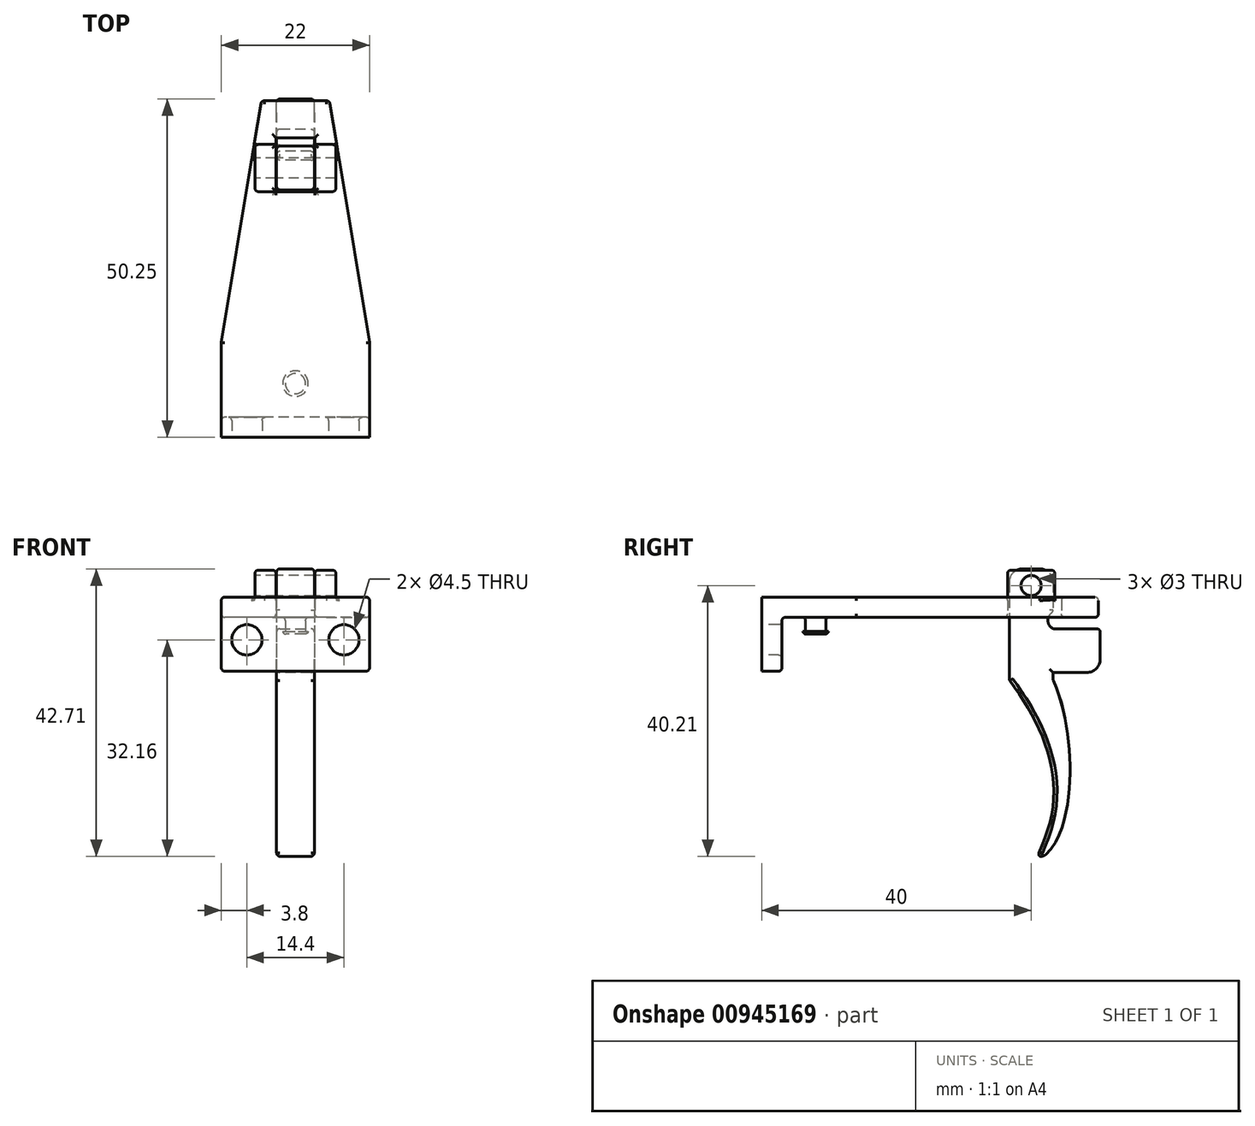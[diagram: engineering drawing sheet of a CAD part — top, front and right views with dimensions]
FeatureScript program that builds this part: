
annotation { "Feature Type Name" : "Feature", "Feature Type Description" : "" }
export const myFeature = defineFeature(function(context is Context, id is Id, definition is map)
    precondition{}
    {
        {
            var Q0;
            Q0=qCreatedBy(makeId("Right.planeOp"),FACE);
            var sketch = newSketch(context, id + "F0", { "sketchPlane" : qUnion([Q0])});
            skLineSegment(sketch, "E0", {"start": v(-37, -4.7) * mm, "end": v(-37, -12.7) * mm});
            skLineSegment(sketch, "E1", {"start": v(-37, -12.7) * mm, "end": v(-40, -12.7) * mm});
            skLineSegment(sketch, "E2", {"start": v(-40, -12.7) * mm, "end": v(-40, -1.7) * mm});
            skLineSegment(sketch, "E3", {"start": v(-40, -1.7) * mm, "end": v(10, -1.7) * mm});
            skLineSegment(sketch, "E4", {"start": v(10, -1.7) * mm, "end": v(10, -4.7) * mm});
            skLineSegment(sketch, "E5", {"start": v(10, -4.7) * mm, "end": v(-37, -4.7) * mm});
            skLineSegment(sketch, "E6", {"start": v(-3.5, -1.7) * mm, "end": v(-3.5, 2.3) * mm});
            skLineSegment(sketch, "E7", {"start": v(-3.5, 2.3) * mm, "end": v(3.5, 2.3) * mm});
            skLineSegment(sketch, "E8", {"start": v(3.5, 2.3) * mm, "end": v(3.5, -1.7) * mm});
            skCircle(sketch, "E9", {"center": v(0, 0) * mm, "radius": 1.5 * mm});
            skLineSegment(sketch, "E10", {"start": v(-33.5, -4.7) * mm, "end": v(-33.5, -6.8) * mm});
            skLineSegment(sketch, "E11", {"start": v(-33.5, -6.8) * mm, "end": v(-33.9, -6.8) * mm});
            skLineSegment(sketch, "E12", {"start": v(-33.9, -6.8) * mm, "end": v(-33.9, -7.2) * mm});
            skLineSegment(sketch, "E13", {"start": v(-33.9, -7.2) * mm, "end": v(-32, -7.2) * mm});
            skPoint(sketch, "E14.startSnap0", {"position": v(-32, -7.2) * mm});
            skLineSegment(sketch, "E15", {"start": v(-33.5, -4.7) * mm, "end": v(-30.5, -4.7) * mm});
            skLineSegment(sketch, "E16", {"start": v(-32, -7.2) * mm, "end": v(-32, -4.7) * mm});
            skSolve(sketch);
        }
        {
            var Q0;
            Q0=qCreatedBy(makeId("Right.planeOp"),FACE);
            var sketch = newSketch(context, id + "F1", { "sketchPlane" : qUnion([Q0])});
            skLineSegment(sketch, "E17", {"start": v(-3.25, 2.5) * mm, "end": v(3.25, 2.5) * mm});
            skLineSegment(sketch, "E18", {"start": v(3.25, 2.5) * mm, "end": v(3.25, -3.9) * mm});
            skLineSegment(sketch, "E19", {"start": v(3.25, -6.4) * mm, "end": v(10.25, -6.4) * mm});
            skLineSegment(sketch, "E20", {"start": v(10.25, -6.4) * mm, "end": v(10.25, -12.9) * mm});
            skLineSegment(sketch, "E21", {"start": v(10.25, -12.9) * mm, "end": v(3.25, -12.9) * mm});
            skLineSegment(sketch, "E22", {"start": v(3.25, -12.9) * mm, "end": v(3.25, -14) * mm});
            skLineSegment(sketch, "E23", {"start": v(-3.25, 2.5) * mm, "end": v(-3.25, -14) * mm});
            skFitSpline(sketch, "E24", {"points": [v(3.25, -14) * mm, v(2.1, -40) * mm], "startDerivative": vector(10.65, -23.23) * mm, "endDerivative": vector(-14.09, -12.06) * mm});
            skLineSegment(sketch, "E25", {"start": v(-3.25, -14) * mm, "end": v(-3.25, -43.38) * mm, "construction": true});
            skLineSegment(sketch, "E26", {"start": v(3.25, -14) * mm, "end": v(3.25, -43.8) * mm, "construction": true});
            skFitSpline(sketch, "E27", {"points": [v(-3.25, -14) * mm, v(1.15, -40) * mm, v(2.1, -40) * mm], "startDerivative": vector(42.39, -56.19) * mm, "endDerivative": vector(10.15, 5.19) * mm});
            skPoint(sketch, "E28", {"position": v(5.75, -28.9) * mm});
            skPoint(sketch, "E28.positionSnap0", {"position": v(3.25, -28.9) * mm});
            skCircle(sketch, "E29", {"center": v(0, 0) * mm, "radius": 1.5 * mm});
            skArc(sketch, "E30", {"start": v(3.25, -3.9) * mm, "mid": v(2.49, -5.15) * mm, "end": v(3.25, -6.4) * mm});
            skLineSegment(sketch, "E31.trimOffspring", {"start": v(3.25, -6.4) * mm, "end": v(3.25, -6.4) * mm});
            skSolve(sketch);
        }
        {
            var Q0;
            Q0=makeQuery(id+"F0.imprint","IMPRINT",FACE,{"disambiguationData":[TD([[makeQuery(id+"F0.imprint","IMPRINT",EDGE,{"derivedFrom":sQuery(id+"F0.wireOp",EDGE,"E0")}),-1.0]])]});
            extrude(context, id + "F2", {"entities" : qUnion([Q0]), "endBound" : BoundingType.SYMMETRIC, "depth" : 22 * mm, "offsetDistance" : 25 * mm});
        }
        {
            var Q0;
            {var subQ1=sQuery(id+"F0.wireOp",EDGE,"E6");Q0=makeQuery(id+"F0.imprint","IMPRINT",FACE,{"disambiguationData":[TD([[makeQuery(id+"F0.imprint","IMPRINT",EDGE,{"derivedFrom":subQ1}),-1.0]])]});}
            extrude(context, id + "F3", {"entities" : qUnion([Q0]), "operationType" : NewBodyOperationType.ADD, "endBound" : BoundingType.SYMMETRIC, "depth" : 12 * mm, "offsetDistance" : 25 * mm});
        }
        {
            var Q0;
            Q0=qCreatedBy(makeId("Right.planeOp"),FACE);
            var sketch = newSketch(context, id + "F4", { "sketchPlane" : qUnion([Q0])});
            skLineSegment(sketch, "E32.bottom", {"start": v(-3.5, 4) * mm, "end": v(4.5, 4) * mm});
            skLineSegment(sketch, "E32.top", {"start": v(-3.5, -6) * mm, "end": v(4.5, -6) * mm});
            skLineSegment(sketch, "E32.left", {"start": v(-3.5, 4) * mm, "end": v(-3.5, -6) * mm});
            skLineSegment(sketch, "E32.right", {"start": v(4.5, 4) * mm, "end": v(4.5, -6) * mm});
            skSolve(sketch);
        }
        {
            var Q0;
            Q0 = qSketchRegion(id + "F4", true);
            extrude(context, id + "F5", {"entities" : qUnion([Q0]), "operationType" : NewBodyOperationType.REMOVE, "endBound" : BoundingType.SYMMETRIC, "depth" : 5.8 * mm, "offsetDistance" : 25 * mm});
        }
        {
            var Q0;
            Q0 = qSketchRegion(id + "F1", true);
            extrude(context, id + "F6", {"entities" : qUnion([Q0]), "endBound" : BoundingType.SYMMETRIC, "depth" : 5.6 * mm, "offsetDistance" : 25 * mm});
        }
        {
            var Q0;
            Q0=makeQuery(id+"F1.imprint","IMPRINT",FACE,{"disambiguationData":[TD([[makeQuery(id+"F1.imprint","IMPRINT",EDGE,{"derivedFrom":sQuery(id+"F1.wireOp",EDGE,"E29")}),1.0]])]});
            extrude(context, id + "F7", {"entities" : qUnion([Q0]), "operationType" : NewBodyOperationType.REMOVE, "endBound" : BoundingType.SYMMETRIC, "depth" : 12 * mm, "offsetDistance" : 25 * mm});
        }
        {
            var Q0;
            Q0=makeQuery(id+"F6.opExtrude","SWEPT_EDGE",EDGE,{"disambiguationData":[OSD([sQuery(id+"F1.wireOp",EDGE,"E17"),sQuery(id+"F1.wireOp",EDGE,"E23")])]});
            var Q1;
            Q1=makeQuery(id+"F6.opExtrude","SWEPT_EDGE",EDGE,{"disambiguationData":[OSD([sQuery(id+"F1.wireOp",EDGE,"E17"),sQuery(id+"F1.wireOp",EDGE,"E18")])]});
            var Q2;
            Q2=makeQuery(id+"F6.opExtrude","SWEPT_EDGE",EDGE,{"disambiguationData":[OSD([sQuery(id+"F1.wireOp",EDGE,"E20"),sQuery(id+"F1.wireOp",EDGE,"E21")])]});
            fillet(context, id + "F8", {"entities" : qUnion([Q0, Q1, Q2]), "radius" : 2 * mm, "tangentPropagation" : true, "allowEdgeOverflow" : false});
        }
        {
            var Q0;
            Q0=makeQuery(id+"F6.opExtrude","CAP_EDGE",EDGE,{"disambiguationData":[OSD([sQuery(id+"F1.wireOp",EDGE,"E23")])],"isStart":true});
            var Q1;
            Q1=makeQuery(id+"F6.opExtrude","CAP_EDGE",EDGE,{"disambiguationData":[OSD([sQuery(id+"F1.wireOp",EDGE,"E27")])],"isStart":false});
            var Q2;
            Q2=makeQuery(id+"F6.opExtrude","CAP_EDGE",EDGE,{"disambiguationData":[OSD([sQuery(id+"F1.wireOp",EDGE,"E27")])],"isStart":true});
            var Q3;
            Q3=makeQuery(id+"F6.opExtrude","CAP_EDGE",EDGE,{"disambiguationData":[OSD([sQuery(id+"F1.wireOp",EDGE,"E24")])],"isStart":false});
            var Q4;
            Q4=makeQuery(id+"F6.opExtrude","CAP_EDGE",EDGE,{"disambiguationData":[OSD([sQuery(id+"F1.wireOp",EDGE,"E24")])],"isStart":true});
            var Q5;
            Q5=makeQuery(id+"F6.opExtrude","SWEPT_EDGE",EDGE,{"disambiguationData":[OSD([sQuery(id+"F1.wireOp",EDGE,"E22"),sQuery(id+"F1.wireOp",EDGE,"E24")])]});
            var Q6;
            Q6=makeQuery(id+"F6.opExtrude","SWEPT_EDGE",EDGE,{"disambiguationData":[OSD([sQuery(id+"F1.wireOp",EDGE,"E24"),sQuery(id+"F1.wireOp",EDGE,"E27")])]});
            var Q7;
            Q7=makeQuery(id+"F6.opExtrude","CAP_EDGE",EDGE,{"disambiguationData":[OSD([sQuery(id+"F1.wireOp",EDGE,"E23")])],"isStart":false});
            var Q8;
            Q8=makeQuery(id+"F6.opExtrude","SWEPT_EDGE",EDGE,{"disambiguationData":[OSD([sQuery(id+"F1.wireOp",EDGE,"E19"),sQuery(id+"F1.wireOp",EDGE,"E20")])]});
            var Q9;
            {var subQ0=sQuery(id+"F1.wireOp",EDGE,"E21");var subQ1=sQuery(id+"F1.wireOp",EDGE,"E20");Q9=makeQuery(id+"F8.opFillet","BLEND_EDGE",EDGE,{"blendedFrom":[makeQuery(id+"F6.opExtrude","SWEPT_EDGE",EDGE,{"disambiguationData":[OSD([subQ1,subQ0])]}),makeQuery(id+"F6.opExtrude","CAP_FACE",FACE,{"disambiguationData":[OSD([sQuery(id+"F1.wireOp",EDGE,"E17"),sQuery(id+"F1.wireOp",EDGE,"E18"),sQuery(id+"F1.wireOp",EDGE,"E19"),subQ1,subQ0,sQuery(id+"F1.wireOp",EDGE,"E22"),sQuery(id+"F1.wireOp",EDGE,"E23"),sQuery(id+"F1.wireOp",EDGE,"E24"),sQuery(id+"F1.wireOp",EDGE,"E27"),sQuery(id+"F1.wireOp",EDGE,"E29")])],"isStart":false})],"blendedInto":[makeQuery(id+"F6.opExtrude","CAP_FACE",FACE,{"disambiguationData":[OSD([sQuery(id+"F1.wireOp",EDGE,"E17"),sQuery(id+"F1.wireOp",EDGE,"E18"),sQuery(id+"F1.wireOp",EDGE,"E19"),subQ1,subQ0,sQuery(id+"F1.wireOp",EDGE,"E22"),sQuery(id+"F1.wireOp",EDGE,"E23"),sQuery(id+"F1.wireOp",EDGE,"E24"),sQuery(id+"F1.wireOp",EDGE,"E27"),sQuery(id+"F1.wireOp",EDGE,"E29")])],"isStart":false})]});}
            var Q10;
            Q10=makeQuery(id+"F6.opExtrude","CAP_EDGE",EDGE,{"disambiguationData":[OSD([sQuery(id+"F1.wireOp",EDGE,"E20")])],"isStart":false});
            var Q11;
            {var subQ0=sQuery(id+"F1.wireOp",EDGE,"E21");var subQ1=sQuery(id+"F1.wireOp",EDGE,"E20");Q11=makeQuery(id+"F8.opFillet","BLEND_EDGE",EDGE,{"blendedFrom":[makeQuery(id+"F6.opExtrude","SWEPT_EDGE",EDGE,{"disambiguationData":[OSD([subQ1,subQ0])]}),makeQuery(id+"F6.opExtrude","CAP_FACE",FACE,{"disambiguationData":[OSD([sQuery(id+"F1.wireOp",EDGE,"E17"),sQuery(id+"F1.wireOp",EDGE,"E18"),sQuery(id+"F1.wireOp",EDGE,"E19"),subQ1,subQ0,sQuery(id+"F1.wireOp",EDGE,"E22"),sQuery(id+"F1.wireOp",EDGE,"E23"),sQuery(id+"F1.wireOp",EDGE,"E24"),sQuery(id+"F1.wireOp",EDGE,"E27"),sQuery(id+"F1.wireOp",EDGE,"E29")])],"isStart":true})],"blendedInto":[makeQuery(id+"F6.opExtrude","CAP_FACE",FACE,{"disambiguationData":[OSD([sQuery(id+"F1.wireOp",EDGE,"E17"),sQuery(id+"F1.wireOp",EDGE,"E18"),sQuery(id+"F1.wireOp",EDGE,"E19"),subQ1,subQ0,sQuery(id+"F1.wireOp",EDGE,"E22"),sQuery(id+"F1.wireOp",EDGE,"E23"),sQuery(id+"F1.wireOp",EDGE,"E24"),sQuery(id+"F1.wireOp",EDGE,"E27"),sQuery(id+"F1.wireOp",EDGE,"E29")])],"isStart":true})]});}
            var Q12;
            {var subQ0=sQuery(id+"F1.wireOp",EDGE,"E17");Q12=makeQuery(id+"F8.opFillet","BLEND_EDGE",EDGE,{"blendedFrom":[makeQuery(id+"F6.opExtrude","SWEPT_EDGE",EDGE,{"disambiguationData":[OSD([subQ0,sQuery(id+"F1.wireOp",EDGE,"E23")])]}),makeQuery(id+"F6.opExtrude","SWEPT_EDGE",EDGE,{"disambiguationData":[OSD([subQ0,sQuery(id+"F1.wireOp",EDGE,"E18")])]})],"blendedInto":[]});}
            var Q13;
            Q13=makeQuery(id+"F7.opExtrude","CAP_EDGE",EDGE,{"disambiguationData":[OSD([sQuery(id+"F1.wireOp",EDGE,"E29")])],"isStart":false});
            var Q14;
            Q14=makeQuery(id+"F7.opExtrude","CAP_EDGE",EDGE,{"disambiguationData":[OSD([sQuery(id+"F1.wireOp",EDGE,"E29")])],"isStart":true});
            var Q15;
            {var subQ1=sQuery(id+"F0.wireOp",EDGE,"E7");var subQ2=sQuery(id+"F0.wireOp",EDGE,"E6");Q15=makeQuery(id+"F5.boolean.opBoolean","SPLIT",EDGE,{"disambiguationData":[TD([makeQuery(id+"F5.opExtrude","CAP_FACE",FACE,{"disambiguationData":[OSD([sQuery(id+"F4.wireOp",EDGE,"E32.bottom"),sQuery(id+"F4.wireOp",EDGE,"E32.top"),sQuery(id+"F4.wireOp",EDGE,"E32.left"),sQuery(id+"F4.wireOp",EDGE,"E32.right")])],"isStart":true})])],"derivedFrom":makeQuery(id+"F3.opExtrude","SWEPT_EDGE",EDGE,{"disambiguationData":[OSD([subQ2,subQ1])]})});}
            var Q16;
            {var subQ1=sQuery(id+"F0.wireOp",EDGE,"E8");var subQ2=sQuery(id+"F0.wireOp",EDGE,"E7");Q16=makeQuery(id+"F5.boolean.opBoolean","SPLIT",EDGE,{"disambiguationData":[TD([makeQuery(id+"F5.opExtrude","CAP_FACE",FACE,{"disambiguationData":[OSD([sQuery(id+"F4.wireOp",EDGE,"E32.bottom"),sQuery(id+"F4.wireOp",EDGE,"E32.top"),sQuery(id+"F4.wireOp",EDGE,"E32.left"),sQuery(id+"F4.wireOp",EDGE,"E32.right")])],"isStart":true})])],"derivedFrom":makeQuery(id+"F3.opExtrude","SWEPT_EDGE",EDGE,{"disambiguationData":[OSD([subQ2,subQ1])]})});}
            var Q17;
            {var subQ1=sQuery(id+"F0.wireOp",EDGE,"E8");var subQ2=sQuery(id+"F0.wireOp",EDGE,"E7");Q17=makeQuery(id+"F5.boolean.opBoolean","SPLIT",EDGE,{"disambiguationData":[TD([makeQuery(id+"F5.opExtrude","CAP_FACE",FACE,{"disambiguationData":[OSD([sQuery(id+"F4.wireOp",EDGE,"E32.bottom"),sQuery(id+"F4.wireOp",EDGE,"E32.top"),sQuery(id+"F4.wireOp",EDGE,"E32.left"),sQuery(id+"F4.wireOp",EDGE,"E32.right")])],"isStart":false})])],"derivedFrom":makeQuery(id+"F3.opExtrude","SWEPT_EDGE",EDGE,{"disambiguationData":[OSD([subQ2,subQ1])]})});}
            var Q18;
            {var subQ1=sQuery(id+"F0.wireOp",EDGE,"E7");var subQ2=sQuery(id+"F0.wireOp",EDGE,"E6");Q18=makeQuery(id+"F5.boolean.opBoolean","SPLIT",EDGE,{"disambiguationData":[TD([makeQuery(id+"F5.opExtrude","CAP_FACE",FACE,{"disambiguationData":[OSD([sQuery(id+"F4.wireOp",EDGE,"E32.bottom"),sQuery(id+"F4.wireOp",EDGE,"E32.top"),sQuery(id+"F4.wireOp",EDGE,"E32.left"),sQuery(id+"F4.wireOp",EDGE,"E32.right")])],"isStart":false})])],"derivedFrom":makeQuery(id+"F3.opExtrude","SWEPT_EDGE",EDGE,{"disambiguationData":[OSD([subQ2,subQ1])]})});}
            var Q19;
            Q19=makeQuery(id+"F3.opExtrude","CAP_EDGE",EDGE,{"disambiguationData":[OSD([sQuery(id+"F0.wireOp",EDGE,"E6")])],"isStart":false});
            var Q20;
            Q20=makeQuery(id+"F3.opExtrude","CAP_EDGE",EDGE,{"disambiguationData":[OSD([sQuery(id+"F0.wireOp",EDGE,"E8")])],"isStart":false});
            var Q21;
            {var subQ0=sQuery(id+"F0.wireOp",EDGE,"E7");Q21=makeQuery(id+"F5.boolean.opBoolean","INTERSECT",EDGE,{"derivedFrom":[makeQuery(id+"F3.opExtrude","SWEPT_FACE",FACE,{"disambiguationData":[OSD([subQ0]),TDD([makeQuery(id+"F0.imprint","IMPRINT",EDGE,{"disambiguationData":[TD([[makeQuery(id+"F0.imprint","INTERSECT",VERTEX,{"derivedFrom":[sQuery(id+"F0.wireOp",EDGE,"E6"),subQ0]}),-1.0]])],"derivedFrom":subQ0})])]}),makeQuery(id+"F5.opExtrude","CAP_FACE",FACE,{"disambiguationData":[OSD([sQuery(id+"F4.wireOp",EDGE,"E32.bottom"),sQuery(id+"F4.wireOp",EDGE,"E32.top"),sQuery(id+"F4.wireOp",EDGE,"E32.left"),sQuery(id+"F4.wireOp",EDGE,"E32.right")])],"isStart":false})]});}
            var Q22;
            {var subQ0=sQuery(id+"F0.wireOp",EDGE,"E7");Q22=makeQuery(id+"F5.boolean.opBoolean","INTERSECT",EDGE,{"derivedFrom":[makeQuery(id+"F3.opExtrude","SWEPT_FACE",FACE,{"disambiguationData":[OSD([subQ0]),TDD([makeQuery(id+"F0.imprint","IMPRINT",EDGE,{"disambiguationData":[TD([[makeQuery(id+"F0.imprint","INTERSECT",VERTEX,{"derivedFrom":[subQ0,sQuery(id+"F0.wireOp",EDGE,"E8")]}),1.0]])],"derivedFrom":subQ0})])]}),makeQuery(id+"F5.opExtrude","CAP_FACE",FACE,{"disambiguationData":[OSD([sQuery(id+"F4.wireOp",EDGE,"E32.bottom"),sQuery(id+"F4.wireOp",EDGE,"E32.top"),sQuery(id+"F4.wireOp",EDGE,"E32.left"),sQuery(id+"F4.wireOp",EDGE,"E32.right")])],"isStart":false})]});}
            var Q23;
            {var subQ0=sQuery(id+"F0.wireOp",EDGE,"E7");Q23=makeQuery(id+"F3.opExtrude","CAP_EDGE",EDGE,{"disambiguationData":[OSD([subQ0]),TDD([makeQuery(id+"F0.imprint","IMPRINT",EDGE,{"disambiguationData":[TD([[makeQuery(id+"F0.imprint","INTERSECT",VERTEX,{"derivedFrom":[subQ0,sQuery(id+"F0.wireOp",EDGE,"E8")]}),1.0]])],"derivedFrom":subQ0})])],"isStart":true});}
            var Q24;
            {var subQ0=sQuery(id+"F1.wireOp",EDGE,"E18");var subQ1=sQuery(id+"F1.wireOp",EDGE,"E17");Q24=makeQuery(id+"F8.opFillet","BLEND_EDGE",EDGE,{"blendedFrom":[makeQuery(id+"F6.opExtrude","SWEPT_EDGE",EDGE,{"disambiguationData":[OSD([subQ1,subQ0])]}),makeQuery(id+"F6.opExtrude","CAP_FACE",FACE,{"disambiguationData":[OSD([subQ1,subQ0,sQuery(id+"F1.wireOp",EDGE,"E19"),sQuery(id+"F1.wireOp",EDGE,"E20"),sQuery(id+"F1.wireOp",EDGE,"E21"),sQuery(id+"F1.wireOp",EDGE,"E22"),sQuery(id+"F1.wireOp",EDGE,"E23"),sQuery(id+"F1.wireOp",EDGE,"E24"),sQuery(id+"F1.wireOp",EDGE,"E27"),sQuery(id+"F1.wireOp",EDGE,"E29")])],"isStart":true})],"blendedInto":[makeQuery(id+"F6.opExtrude","CAP_FACE",FACE,{"disambiguationData":[OSD([subQ1,subQ0,sQuery(id+"F1.wireOp",EDGE,"E19"),sQuery(id+"F1.wireOp",EDGE,"E20"),sQuery(id+"F1.wireOp",EDGE,"E21"),sQuery(id+"F1.wireOp",EDGE,"E22"),sQuery(id+"F1.wireOp",EDGE,"E23"),sQuery(id+"F1.wireOp",EDGE,"E24"),sQuery(id+"F1.wireOp",EDGE,"E27"),sQuery(id+"F1.wireOp",EDGE,"E29")])],"isStart":true})]});}
            var Q25;
            {var subQ0=sQuery(id+"F0.wireOp",EDGE,"E7");Q25=makeQuery(id+"F3.opExtrude","CAP_EDGE",EDGE,{"disambiguationData":[OSD([subQ0]),TDD([makeQuery(id+"F0.imprint","IMPRINT",EDGE,{"disambiguationData":[TD([[makeQuery(id+"F0.imprint","INTERSECT",VERTEX,{"derivedFrom":[sQuery(id+"F0.wireOp",EDGE,"E6"),subQ0]}),-1.0]])],"derivedFrom":subQ0})])],"isStart":true});}
            var Q26;
            {var subQ0=sQuery(id+"F0.wireOp",EDGE,"E7");Q26=makeQuery(id+"F5.boolean.opBoolean","INTERSECT",EDGE,{"derivedFrom":[makeQuery(id+"F3.opExtrude","SWEPT_FACE",FACE,{"disambiguationData":[OSD([subQ0]),TDD([makeQuery(id+"F0.imprint","IMPRINT",EDGE,{"disambiguationData":[TD([[makeQuery(id+"F0.imprint","INTERSECT",VERTEX,{"derivedFrom":[sQuery(id+"F0.wireOp",EDGE,"E6"),subQ0]}),-1.0]])],"derivedFrom":subQ0})])]}),makeQuery(id+"F5.opExtrude","CAP_FACE",FACE,{"disambiguationData":[OSD([sQuery(id+"F4.wireOp",EDGE,"E32.bottom"),sQuery(id+"F4.wireOp",EDGE,"E32.top"),sQuery(id+"F4.wireOp",EDGE,"E32.left"),sQuery(id+"F4.wireOp",EDGE,"E32.right")])],"isStart":true})]});}
            var Q27;
            Q27=makeQuery(id+"F3.opExtrude","CAP_EDGE",EDGE,{"disambiguationData":[OSD([sQuery(id+"F0.wireOp",EDGE,"E6")])],"isStart":true});
            var Q28;
            Q28=makeQuery(id+"F3.opExtrude","CAP_EDGE",EDGE,{"disambiguationData":[OSD([sQuery(id+"F0.wireOp",EDGE,"E8")])],"isStart":true});
            var Q29;
            {var subQ0=sQuery(id+"F0.wireOp",EDGE,"E7");Q29=makeQuery(id+"F5.boolean.opBoolean","INTERSECT",EDGE,{"derivedFrom":[makeQuery(id+"F3.opExtrude","SWEPT_FACE",FACE,{"disambiguationData":[OSD([subQ0]),TDD([makeQuery(id+"F0.imprint","IMPRINT",EDGE,{"disambiguationData":[TD([[makeQuery(id+"F0.imprint","INTERSECT",VERTEX,{"derivedFrom":[subQ0,sQuery(id+"F0.wireOp",EDGE,"E8")]}),1.0]])],"derivedFrom":subQ0})])]}),makeQuery(id+"F5.opExtrude","CAP_FACE",FACE,{"disambiguationData":[OSD([sQuery(id+"F4.wireOp",EDGE,"E32.bottom"),sQuery(id+"F4.wireOp",EDGE,"E32.top"),sQuery(id+"F4.wireOp",EDGE,"E32.left"),sQuery(id+"F4.wireOp",EDGE,"E32.right")])],"isStart":true})]});}
            var Q30;
            Q30=makeQuery(id+"F5.boolean.opBoolean","INTERSECT",EDGE,{"derivedFrom":[makeQuery(id+"F2.opExtrude","SWEPT_FACE",FACE,{"disambiguationData":[OSD([sQuery(id+"F0.wireOp",EDGE,"E3")])]}),makeQuery(id+"F5.opExtrude","SWEPT_FACE",FACE,{"disambiguationData":[OSD([sQuery(id+"F4.wireOp",EDGE,"E32.right")])]})]});
            var Q31;
            Q31=makeQuery(id+"F5.boolean.opBoolean","INTERSECT",EDGE,{"derivedFrom":[makeQuery(id+"F2.opExtrude","SWEPT_FACE",FACE,{"disambiguationData":[OSD([sQuery(id+"F0.wireOp",EDGE,"E3")])]}),makeQuery(id+"F5.opExtrude","SWEPT_FACE",FACE,{"disambiguationData":[OSD([sQuery(id+"F4.wireOp",EDGE,"E32.left")])]})]});
            var Q32;
            Q32=makeQuery(id+"F5.boolean.opBoolean","INTERSECT",EDGE,{"disambiguationData":[OD(0.0)],"derivedFrom":[makeQuery(id+"F2.opExtrude","SWEPT_FACE",FACE,{"disambiguationData":[OSD([sQuery(id+"F0.wireOp",EDGE,"E3")])]}),makeQuery(id+"F5.opExtrude","CAP_FACE",FACE,{"disambiguationData":[OSD([sQuery(id+"F4.wireOp",EDGE,"E32.bottom"),sQuery(id+"F4.wireOp",EDGE,"E32.top"),sQuery(id+"F4.wireOp",EDGE,"E32.left"),sQuery(id+"F4.wireOp",EDGE,"E32.right")])],"isStart":true})]});
            var Q33;
            Q33=makeQuery(id+"F5.boolean.opBoolean","INTERSECT",EDGE,{"disambiguationData":[OD(1.0)],"derivedFrom":[makeQuery(id+"F2.opExtrude","SWEPT_FACE",FACE,{"disambiguationData":[OSD([sQuery(id+"F0.wireOp",EDGE,"E3")])]}),makeQuery(id+"F5.opExtrude","CAP_FACE",FACE,{"disambiguationData":[OSD([sQuery(id+"F4.wireOp",EDGE,"E32.bottom"),sQuery(id+"F4.wireOp",EDGE,"E32.top"),sQuery(id+"F4.wireOp",EDGE,"E32.left"),sQuery(id+"F4.wireOp",EDGE,"E32.right")])],"isStart":true})]});
            var Q34;
            Q34=makeQuery(id+"F5.boolean.opBoolean","INTERSECT",EDGE,{"disambiguationData":[OD(1.0)],"derivedFrom":[makeQuery(id+"F2.opExtrude","SWEPT_FACE",FACE,{"disambiguationData":[OSD([sQuery(id+"F0.wireOp",EDGE,"E3")])]}),makeQuery(id+"F5.opExtrude","CAP_FACE",FACE,{"disambiguationData":[OSD([sQuery(id+"F4.wireOp",EDGE,"E32.bottom"),sQuery(id+"F4.wireOp",EDGE,"E32.top"),sQuery(id+"F4.wireOp",EDGE,"E32.left"),sQuery(id+"F4.wireOp",EDGE,"E32.right")])],"isStart":false})]});
            var Q35;
            Q35=makeQuery(id+"F2.opExtrude","CAP_EDGE",EDGE,{"disambiguationData":[OSD([sQuery(id+"F0.wireOp",EDGE,"E0")])],"isStart":false});
            var Q36;
            Q36=makeQuery(id+"F2.opExtrude","CAP_EDGE",EDGE,{"disambiguationData":[OSD([sQuery(id+"F0.wireOp",EDGE,"E5")])],"isStart":false});
            var Q37;
            Q37=makeQuery(id+"F2.opExtrude","CAP_EDGE",EDGE,{"disambiguationData":[OSD([sQuery(id+"F0.wireOp",EDGE,"E3")])],"isStart":false});
            var Q38;
            Q38=makeQuery(id+"F2.opExtrude","CAP_EDGE",EDGE,{"disambiguationData":[OSD([sQuery(id+"F0.wireOp",EDGE,"E3")])],"isStart":true});
            var Q39;
            Q39=makeQuery(id+"F2.opExtrude","SWEPT_EDGE",EDGE,{"disambiguationData":[OSD([sQuery(id+"F0.wireOp",EDGE,"E3"),sQuery(id+"F0.wireOp",EDGE,"E4")])]});
            var Q40;
            Q40=makeQuery(id+"F2.opExtrude","SWEPT_EDGE",EDGE,{"disambiguationData":[OSD([sQuery(id+"F0.wireOp",EDGE,"E4"),sQuery(id+"F0.wireOp",EDGE,"E5")])]});
            var Q41;
            Q41=makeQuery(id+"F2.opExtrude","SWEPT_EDGE",EDGE,{"disambiguationData":[OSD([sQuery(id+"F0.wireOp",EDGE,"E0"),sQuery(id+"F0.wireOp",EDGE,"E5")])]});
            var Q42;
            Q42=makeQuery(id+"F2.opExtrude","SWEPT_EDGE",EDGE,{"disambiguationData":[OSD([sQuery(id+"F0.wireOp",EDGE,"E0"),sQuery(id+"F0.wireOp",EDGE,"E1")])]});
            var Q43;
            Q43=makeQuery(id+"F2.opExtrude","CAP_EDGE",EDGE,{"disambiguationData":[OSD([sQuery(id+"F0.wireOp",EDGE,"E1")])],"isStart":false});
            var Q44;
            Q44=makeQuery(id+"F2.opExtrude","CAP_EDGE",EDGE,{"disambiguationData":[OSD([sQuery(id+"F0.wireOp",EDGE,"E1")])],"isStart":true});
            var Q45;
            Q45=makeQuery(id+"F2.opExtrude","CAP_EDGE",EDGE,{"disambiguationData":[OSD([sQuery(id+"F0.wireOp",EDGE,"E4")])],"isStart":true});
            var Q46;
            Q46=makeQuery(id+"F2.opExtrude","CAP_EDGE",EDGE,{"disambiguationData":[OSD([sQuery(id+"F0.wireOp",EDGE,"E4")])],"isStart":false});
            var Q47;
            Q47=makeQuery(id+"F2.opExtrude","CAP_EDGE",EDGE,{"disambiguationData":[OSD([sQuery(id+"F0.wireOp",EDGE,"E0")])],"isStart":true});
            var Q48;
            Q48=makeQuery(id+"F6.opExtrude","SWEPT_EDGE",EDGE,{"disambiguationData":[OSD([sQuery(id+"F1.wireOp",EDGE,"E19"),sQuery(id+"F1.wireOp",EDGE,"E31.trimOffspring")])]});
            var Q49;
            Q49=makeQuery(id+"F6.opExtrude","SWEPT_EDGE",EDGE,{"disambiguationData":[OSD([sQuery(id+"F1.wireOp",EDGE,"E19"),sQuery(id+"F1.wireOp",EDGE,"E20")])]});
            var Q50;
            Q50=makeQuery(id+"F3.opExtrude","CAP_EDGE",EDGE,{"disambiguationData":[OSD([sQuery(id+"F0.wireOp",EDGE,"E7")])],"isStart":false});
            fillet(context, id + "F9", {"entities" : qUnion([Q0, Q1, Q2, Q3, Q4, Q5, Q6, Q7, Q8, Q9, Q10, Q11, Q12, Q13, Q14, Q15, Q16, Q17, Q18, Q19, Q20, Q21, Q22, Q23, Q24, Q25, Q26, Q27, Q28, Q29, Q30, Q31, Q32, Q33, Q34, Q35, Q36, Q37, Q38, Q39, Q40, Q41, Q42, Q43, Q44, Q45, Q46, Q47, Q48, Q49, Q50]), "radius" : 0.5 * mm, "tangentPropagation" : true, "allowEdgeOverflow" : false});
        }
        {
            var Q0;
            Q0=makeQuery(id+"F5.boolean.opBoolean","INTERSECT",EDGE,{"derivedFrom":[makeQuery(id+"F2.opExtrude","SWEPT_FACE",FACE,{"disambiguationData":[OSD([sQuery(id+"F0.wireOp",EDGE,"E5")])]}),makeQuery(id+"F5.opExtrude","SWEPT_FACE",FACE,{"disambiguationData":[OSD([sQuery(id+"F4.wireOp",EDGE,"E32.left")])]})]});
            var Q1;
            Q1=makeQuery(id+"F5.boolean.opBoolean","INTERSECT",EDGE,{"derivedFrom":[makeQuery(id+"F2.opExtrude","SWEPT_FACE",FACE,{"disambiguationData":[OSD([sQuery(id+"F0.wireOp",EDGE,"E5")])]}),makeQuery(id+"F5.opExtrude","CAP_FACE",FACE,{"disambiguationData":[OSD([sQuery(id+"F4.wireOp",EDGE,"E32.bottom"),sQuery(id+"F4.wireOp",EDGE,"E32.top"),sQuery(id+"F4.wireOp",EDGE,"E32.left"),sQuery(id+"F4.wireOp",EDGE,"E32.right")])],"isStart":false})]});
            var Q2;
            Q2=makeQuery(id+"F5.boolean.opBoolean","INTERSECT",EDGE,{"derivedFrom":[makeQuery(id+"F2.opExtrude","SWEPT_FACE",FACE,{"disambiguationData":[OSD([sQuery(id+"F0.wireOp",EDGE,"E5")])]}),makeQuery(id+"F5.opExtrude","CAP_FACE",FACE,{"disambiguationData":[OSD([sQuery(id+"F4.wireOp",EDGE,"E32.bottom"),sQuery(id+"F4.wireOp",EDGE,"E32.top"),sQuery(id+"F4.wireOp",EDGE,"E32.left"),sQuery(id+"F4.wireOp",EDGE,"E32.right")])],"isStart":true})]});
            var Q3;
            Q3=makeQuery(id+"F6.opExtrude","SWEPT_EDGE",EDGE,{"disambiguationData":[OSD([sQuery(id+"F1.wireOp",EDGE,"E23"),sQuery(id+"F1.wireOp",EDGE,"E27")])]});
            var Q4;
            Q4=makeQuery(id+"F6.opExtrude","CAP_EDGE",EDGE,{"disambiguationData":[OSD([sQuery(id+"F1.wireOp",EDGE,"E27")])],"isStart":false});
            var Q5;
            Q5=makeQuery(id+"F6.opExtrude","CAP_EDGE",EDGE,{"disambiguationData":[OSD([sQuery(id+"F1.wireOp",EDGE,"E27")])],"isStart":true});
            var Q6;
            Q6=makeQuery(id+"F6.opExtrude","CAP_EDGE",EDGE,{"disambiguationData":[OSD([sQuery(id+"F1.wireOp",EDGE,"E24")])],"isStart":false});
            var Q7;
            Q7=makeQuery(id+"F6.opExtrude","CAP_EDGE",EDGE,{"disambiguationData":[OSD([sQuery(id+"F1.wireOp",EDGE,"E24")])],"isStart":true});
            var Q8;
            Q8=makeQuery(id+"F6.opExtrude","CAP_EDGE",EDGE,{"disambiguationData":[OSD([sQuery(id+"F1.wireOp",EDGE,"E23")])],"isStart":false});
            var Q9;
            Q9=makeQuery(id+"F6.opExtrude","CAP_EDGE",EDGE,{"disambiguationData":[OSD([sQuery(id+"F1.wireOp",EDGE,"E23")])],"isStart":true});
            var Q10;
            {var subQ0=sQuery(id+"F1.wireOp",EDGE,"E21");var subQ1=sQuery(id+"F1.wireOp",EDGE,"E20");Q10=makeQuery(id+"F8.opFillet","BLEND_EDGE",EDGE,{"blendedFrom":[makeQuery(id+"F6.opExtrude","SWEPT_EDGE",EDGE,{"disambiguationData":[OSD([subQ1,subQ0])]}),makeQuery(id+"F6.opExtrude","CAP_FACE",FACE,{"disambiguationData":[OSD([sQuery(id+"F1.wireOp",EDGE,"E17"),sQuery(id+"F1.wireOp",EDGE,"E18"),sQuery(id+"F1.wireOp",EDGE,"E19"),subQ1,subQ0,sQuery(id+"F1.wireOp",EDGE,"E22"),sQuery(id+"F1.wireOp",EDGE,"E23"),sQuery(id+"F1.wireOp",EDGE,"E24"),sQuery(id+"F1.wireOp",EDGE,"E27"),sQuery(id+"F1.wireOp",EDGE,"E29"),sQuery(id+"F1.wireOp",EDGE,"E30"),sQuery(id+"F1.wireOp",EDGE,"E31.trimOffspring")])],"isStart":false})],"blendedInto":[makeQuery(id+"F6.opExtrude","CAP_FACE",FACE,{"disambiguationData":[OSD([sQuery(id+"F1.wireOp",EDGE,"E17"),sQuery(id+"F1.wireOp",EDGE,"E18"),sQuery(id+"F1.wireOp",EDGE,"E19"),subQ1,subQ0,sQuery(id+"F1.wireOp",EDGE,"E22"),sQuery(id+"F1.wireOp",EDGE,"E23"),sQuery(id+"F1.wireOp",EDGE,"E24"),sQuery(id+"F1.wireOp",EDGE,"E27"),sQuery(id+"F1.wireOp",EDGE,"E29"),sQuery(id+"F1.wireOp",EDGE,"E30"),sQuery(id+"F1.wireOp",EDGE,"E31.trimOffspring")])],"isStart":false})]});}
            var Q11;
            {var subQ0=sQuery(id+"F1.wireOp",EDGE,"E21");var subQ1=sQuery(id+"F1.wireOp",EDGE,"E20");Q11=makeQuery(id+"F8.opFillet","BLEND_EDGE",EDGE,{"blendedFrom":[makeQuery(id+"F6.opExtrude","SWEPT_EDGE",EDGE,{"disambiguationData":[OSD([subQ1,subQ0])]}),makeQuery(id+"F6.opExtrude","CAP_FACE",FACE,{"disambiguationData":[OSD([sQuery(id+"F1.wireOp",EDGE,"E17"),sQuery(id+"F1.wireOp",EDGE,"E18"),sQuery(id+"F1.wireOp",EDGE,"E19"),subQ1,subQ0,sQuery(id+"F1.wireOp",EDGE,"E22"),sQuery(id+"F1.wireOp",EDGE,"E23"),sQuery(id+"F1.wireOp",EDGE,"E24"),sQuery(id+"F1.wireOp",EDGE,"E27"),sQuery(id+"F1.wireOp",EDGE,"E29"),sQuery(id+"F1.wireOp",EDGE,"E30"),sQuery(id+"F1.wireOp",EDGE,"E31.trimOffspring")])],"isStart":true})],"blendedInto":[makeQuery(id+"F6.opExtrude","CAP_FACE",FACE,{"disambiguationData":[OSD([sQuery(id+"F1.wireOp",EDGE,"E17"),sQuery(id+"F1.wireOp",EDGE,"E18"),sQuery(id+"F1.wireOp",EDGE,"E19"),subQ1,subQ0,sQuery(id+"F1.wireOp",EDGE,"E22"),sQuery(id+"F1.wireOp",EDGE,"E23"),sQuery(id+"F1.wireOp",EDGE,"E24"),sQuery(id+"F1.wireOp",EDGE,"E27"),sQuery(id+"F1.wireOp",EDGE,"E29"),sQuery(id+"F1.wireOp",EDGE,"E30"),sQuery(id+"F1.wireOp",EDGE,"E31.trimOffspring")])],"isStart":true})]});}
            var Q12;
            Q12=makeQuery(id+"F6.opExtrude","CAP_EDGE",EDGE,{"disambiguationData":[OSD([sQuery(id+"F1.wireOp",EDGE,"E22")])],"isStart":false});
            var Q13;
            Q13=makeQuery(id+"F6.opExtrude","CAP_EDGE",EDGE,{"disambiguationData":[OSD([sQuery(id+"F1.wireOp",EDGE,"E22")])],"isStart":true});
            var Q14;
            Q14=makeQuery(id+"F2.opExtrude","SWEPT_FACE",FACE,{"disambiguationData":[OSD([sQuery(id+"F0.wireOp",EDGE,"E0")])]});
            fillet(context, id + "F10", {"entities" : qUnion([Q0, Q1, Q2, Q3, Q4, Q5, Q6, Q7, Q8, Q9, Q10, Q11, Q12, Q13, Q14]), "radius" : 0.5 * mm, "tangentPropagation" : true, "allowEdgeOverflow" : false});
        }
        {
            var Q0;
            {var subQ0=sQuery(id+"F0.wireOp",EDGE,"E10");Q0=makeQuery(id+"F0.imprint","IMPRINT",FACE,{"disambiguationData":[TD([[makeQuery(id+"F0.imprint","IMPRINT",EDGE,{"derivedFrom":subQ0}),1.0]])]});}
            var Q1;
            Q1=sQuery(id+"F0.wireOp",EDGE,"E16");
            revolve(context, id + "F11", {"operationType" : NewBodyOperationType.ADD, "surfaceOperationType" : NewSurfaceOperationType.NEW, "entities" : qUnion([Q0]), "axis" : qUnion([Q1]), "revolveType" : RevolveType.FULL});
        }
        {
            var Q0;
            Q0=makeQuery(id+"F11.opRevolve","SWEPT_EDGE",EDGE,{"disambiguationData":[OSD([sQuery(id+"F0.wireOp",EDGE,"E12"),sQuery(id+"F0.wireOp",EDGE,"E13")])]});
            var Q1;
            Q1=makeQuery(id+"F2.opExtrude","SWEPT_FACE",FACE,{"disambiguationData":[OSD([sQuery(id+"F0.wireOp",EDGE,"E5"),sQuery(id+"F0.wireOp",EDGE,"E15")])]});
            fillet(context, id + "F12", {"entities" : qUnion([Q0, Q1]), "radius" : 0.5 * mm, "tangentPropagation" : true, "allowEdgeOverflow" : false});
        }
        {
            var Q0;
            Q0=makeQuery(id+"F6.opExtrude","CAP_EDGE",EDGE,{"disambiguationData":[OSD([sQuery(id+"F1.wireOp",EDGE,"E30")])],"isStart":true});
            var Q1;
            Q1=makeQuery(id+"F6.opExtrude","CAP_EDGE",EDGE,{"disambiguationData":[OSD([sQuery(id+"F1.wireOp",EDGE,"E30")])],"isStart":false});
            var Q2;
            Q2=makeQuery(id+"F6.opExtrude","CAP_EDGE",EDGE,{"disambiguationData":[OSD([sQuery(id+"F1.wireOp",EDGE,"E18")])],"isStart":true});
            var Q3;
            Q3=makeQuery(id+"F6.opExtrude","CAP_EDGE",EDGE,{"disambiguationData":[OSD([sQuery(id+"F1.wireOp",EDGE,"E18")])],"isStart":false});
            fillet(context, id + "F13", {"entities" : qUnion([Q0, Q1, Q2, Q3]), "radius" : 0.5 * mm, "tangentPropagation" : true, "allowEdgeOverflow" : false});
        }
        {
            var Q0;
            Q0=makeQuery(id+"F2.opExtrude","SWEPT_FACE",FACE,{"disambiguationData":[OSD([sQuery(id+"F0.wireOp",EDGE,"E2")])]});
            var sketch = newSketch(context, id + "F14", { "sketchPlane" : qUnion([Q0])});
            skCircle(sketch, "E33", {"center": v(-7.2, -8.05) * mm, "radius": 2.25 * mm});
            skCircle(sketch, "E34.MirrorC", {"center": v(7.2, -8.05) * mm, "radius": 2.25 * mm});
            skSolve(sketch);
        }
        {
            var Q0;
            Q0 = qSketchRegion(id + "F14", true);
            extrude(context, id + "F15", {"entities" : qUnion([Q0]), "operationType" : NewBodyOperationType.REMOVE, "oppositeDirection" : true, "depth" : 5 * mm, "offsetDistance" : 25 * mm});
        }
        {
            var Q0;
            Q0=makeQuery(id+"F15.boolean.opBoolean","INTERSECT",EDGE,{"derivedFrom":[makeQuery(id+"F2.opExtrude","SWEPT_FACE",FACE,{"disambiguationData":[OSD([sQuery(id+"F0.wireOp",EDGE,"E0")])]}),makeQuery(id+"F15.opExtrude","SWEPT_FACE",FACE,{"disambiguationData":[OSD([sQuery(id+"F14.wireOp",EDGE,"E34.MirrorC")])]})]});
            var Q1;
            Q1=makeQuery(id+"F15.boolean.opBoolean","INTERSECT",EDGE,{"derivedFrom":[makeQuery(id+"F2.opExtrude","SWEPT_FACE",FACE,{"disambiguationData":[OSD([sQuery(id+"F0.wireOp",EDGE,"E0")])]}),makeQuery(id+"F15.opExtrude","SWEPT_FACE",FACE,{"disambiguationData":[OSD([sQuery(id+"F14.wireOp",EDGE,"E33")])]})]});
            var Q2;
            Q2=makeQuery(id+"F2.opExtrude","CAP_EDGE",EDGE,{"disambiguationData":[OSD([sQuery(id+"F0.wireOp",EDGE,"E1")])],"isStart":false});
            var Q3;
            Q3=makeQuery(id+"F2.opExtrude","CAP_EDGE",EDGE,{"disambiguationData":[OSD([sQuery(id+"F0.wireOp",EDGE,"E1")])],"isStart":true});
            fillet(context, id + "F16", {"entities" : qUnion([Q0, Q1, Q2, Q3]), "radius" : .5 * mm, "tangentPropagation" : true, "allowEdgeOverflow" : false});
        }
        {
            var Q0;
            Q0=makeQuery(id+"F2.opExtrude","SWEPT_FACE",FACE,{"disambiguationData":[OSD([sQuery(id+"F0.wireOp",EDGE,"E5"),sQuery(id+"F0.wireOp",EDGE,"E15")])]});
            var sketch = newSketch(context, id + "F17", { "sketchPlane" : qUnion([Q0])});
            skLineSegment(sketch, "E35.bottom", {"start": v(2, -5) * mm, "end": v(-2, -5) * mm});
            skLineSegment(sketch, "E35.top", {"start": v(2, -9) * mm, "end": v(-2, -9) * mm});
            skLineSegment(sketch, "E35.left", {"start": v(2, -5) * mm, "end": v(2, -9) * mm});
            skLineSegment(sketch, "E35.right", {"start": v(-2, -5) * mm, "end": v(-2, -9) * mm});
            skCircle(sketch, "E36", {"center": v(0, -7) * mm, "radius": 0.75 * mm});
            skSolve(sketch);
        }
        {
            var Q0;
            Q0=makeQuery(id+"F2.opExtrude","SWEPT_FACE",FACE,{"disambiguationData":[OSD([sQuery(id+"F0.wireOp",EDGE,"E3")])]});
            var sketch = newSketch(context, id + "F18", { "sketchPlane" : qUnion([Q0])});
            skLineSegment(sketch, "E37", {"start": v(-13.32, 11.48) * mm, "end": v(-13.32, -39.91) * mm});
            skLineSegment(sketch, "E38", {"start": v(-13.32, -39.91) * mm, "end": v(-4.72, 12) * mm});
            skLineSegment(sketch, "E39", {"start": v(-4.72, 12) * mm, "end": v(-13.32, 11.48) * mm});
            skLineSegment(sketch, "E40.MirrorCS", {"start": v(13.32, -39.91) * mm, "end": v(4.72, 12) * mm});
            skLineSegment(sketch, "E41.MirrorCS", {"start": v(13.32, 11.48) * mm, "end": v(13.32, -39.91) * mm});
            skLineSegment(sketch, "E42.MirrorCS", {"start": v(4.72, 12) * mm, "end": v(13.32, 11.48) * mm});
            skSolve(sketch);
        }
        {
            var Q0;
            Q0 = qSketchRegion(id + "F18", true);
            extrude(context, id + "F19", {"entities" : qUnion([Q0]), "operationType" : NewBodyOperationType.REMOVE, "oppositeDirection" : true, "depth" : 5 * mm, "offsetDistance" : 25 * mm});
        }
        {
            var Q0;
            Q0=makeQuery(id+"F19.boolean.opBoolean","COPY",EDGE,{"derivedFrom":makeQuery(id+"F19.opExtrude","CAP_EDGE",EDGE,{"disambiguationData":[OSD([sQuery(id+"F18.wireOp",EDGE,"E40.MirrorCS")])],"isStart":true})});
            var Q1;
            Q1=makeQuery(id+"F19.boolean.opBoolean","INTERSECT",EDGE,{"derivedFrom":[makeQuery(id+"F2.opExtrude","SWEPT_FACE",FACE,{"disambiguationData":[OSD([sQuery(id+"F0.wireOp",EDGE,"E5"),sQuery(id+"F0.wireOp",EDGE,"E15")])]}),makeQuery(id+"F19.opExtrude","SWEPT_FACE",FACE,{"disambiguationData":[OSD([sQuery(id+"F18.wireOp",EDGE,"E40.MirrorCS")])]})]});
            var Q2;
            Q2=makeQuery(id+"F19.boolean.opBoolean","COPY",EDGE,{"derivedFrom":makeQuery(id+"F19.opExtrude","CAP_EDGE",EDGE,{"disambiguationData":[OSD([sQuery(id+"F18.wireOp",EDGE,"E38")])],"isStart":true})});
            var Q3;
            Q3=makeQuery(id+"F19.boolean.opBoolean","INTERSECT",EDGE,{"derivedFrom":[makeQuery(id+"F2.opExtrude","SWEPT_FACE",FACE,{"disambiguationData":[OSD([sQuery(id+"F0.wireOp",EDGE,"E5"),sQuery(id+"F0.wireOp",EDGE,"E15")])]}),makeQuery(id+"F19.opExtrude","SWEPT_FACE",FACE,{"disambiguationData":[OSD([sQuery(id+"F18.wireOp",EDGE,"E38")])]})]});
            fillet(context, id + "F20", {"entities" : qUnion([Q0, Q1, Q2, Q3]), "radius" : 0.5 * mm, "tangentPropagation" : true, "allowEdgeOverflow" : false});
        }
    });
